# Revit family: FU_Inspec_Grade_2-8
name_source: partatom
category: Furniture
units: mm (PartAtom-declared; Revit-internal decimal feet)

## family parameters
Always vertical = Yes
Cut with Voids When Loaded = No
OmniClass Number = 23.40.20.00
OmniClass Title = General Furniture and Specialties
Room Calculation Point = No
Shared = No
Work Plane-Based = No

## types (3) — shared parameters
Assembly Code = E2020
Depth = 780 mm  [stored 2.55906 ft]
Height = 540 mm  [stored 1.77165 ft]
Keynote = 46.B
Manufacturer = Inspec
URL = https://inspecfurniture.com
Weight = 5.0
Width = 580 mm  [stored 1.90289 ft]
zero-valued in all types: Default Elevation

## per-type parameters (varying)
| type | Armrest Material | Description | Frame Material | Model | Seat Material | Seat Pad Material |
| Grade 2.7 - Chrome - Black | Plastic - Black | Armchair with recycled polypropylene seat on a powder coated or chromium plated tubular steel sled based frame. Stackable and linkable | Metal - Chrome - Polished | Grade 2.7 | Colour - Coated - Black | Fabric - Divina Black |
| Grade 2.8 - Red - Red | Plastic - Black | Armchair with recycled polypropylene seat on a powder coated or chromium plated tubular steel sled based frame. With Upholstered seat pad. Stackable and linkable (armchair-chair-armchair) | Colour - Coated - Dark red | Grade 2.8 | Colour - Coated - Dark red | Fabric - Divina Red |
| Grade 2.9 - Grey - Beige | Plastic - White | Armchair with fully upholstered recycled polypropylene seat on a powder coated or chromium plated tubular steel sled based frame. Stackable and linkable | Colour - Coated - Grey | Grade 2.9 | Fabric - Divina Beige | Fabric - Divina Beige |

note: [stored X ft] marks values corroborated as IEEE doubles in the binary element streams (Revit-internal decimal feet)

## geometry (parser evidence)
native form markers: Blend x442, Sweep x2
no freeform markers — native parametric forms only
